# Revit family: Power-ModularDevices-GEWISS-90AM-ENERGY_METER_DIGITAL_THREE_PHASE
name_source: partatom
category: Apparecchi elettrici
revit_build: Autodesk Revit 2016 (Build: 20161004_0715(x64)
units: mm (PartAtom-declared; Revit-internal decimal feet)

## family parameters
Condiviso = No
Host = Superficie
Mantenere orientamento annotazione = Sì
Numero OmniClass = 23.80.30.00
Punto di calcolo locali = Sì
Quota connettore circolare = Usa diametro
Taglio con vuoti quando caricato = No
Tipo di parte = Normale
Titolo OmniClass = Distribution Devices

## types (4) — shared parameters
A = 18 mm  [stored 0.0590551 ft]
Accuracy rate = 1 (active energy) 2 (reactive energy)
B = 85 mm  [stored 0.278871 ft]
C = 59 mm  [stored 0.19357 ft]
Catalogue = POWER
Catalogue Range = 90 AM
D = 45 mm  [stored 0.147638 ft]
Electrocod = 163
Fin_Amperometro = <Per categoria>
IDF = e69c6942-c351-426b-8c99-b51ee961c434
IDT = afdb2495-6e31-48e6-913b-854a097ff101
Immagine tipo = GWD6808.jpg
No. Chorus modules = 4
Numero poli = 3
Potenza in Watt = 0 V
Produttore = GEWISS S.p.A.
Prospetto di default = 1219 mm
Rated voltage = 400Vac
TIPO = 90AM CONTATORI DI ENERGIA TRIFASE DIGITALE_GENERICO : GWD6808 - CONTATORE ENERGIA TRIF.INDIR.TA/5A 4M
Technical sheet = https://www.gewiss.com
URL = https://www.gewiss.com
Version file RFA = 18.0

## per-type parameters (varying)
| type | Descrizione | EAN code | Insertion | Modello |
| GWD6809 - MID THREE PHASE METER INDIR. CT/5A 4M | MID THREE PHASE METER INDIR. CT/5A 4M | 8011564886780 | With TA/5A | GWD6809 |
| GWD6808 - THREE PHASE ENERGY METER INDIR. CT/5A 4M | THREE PHASE ENERGY METER INDIR. CT/5A 4M | 8011564833920 | With TA/5A | GWD6808 |
| GWD6807 - MID THREE PHASE METER DIRECT 80A 4M | MID THREE PHASE METER DIRECT 80A 4M | 8011564886773 | Direct (Imax=80A) | GWD6807 |
| GWD6806 - THREE PHASE ENERGY METER DIRECT 80A 4M | THREE PHASE ENERGY METER DIRECT 80A 4M | 8011564833913 | Direct (Imax=80A) | GWD6806 |

note: [stored X ft] marks values corroborated as IEEE doubles in the binary element streams (Revit-internal decimal feet)
